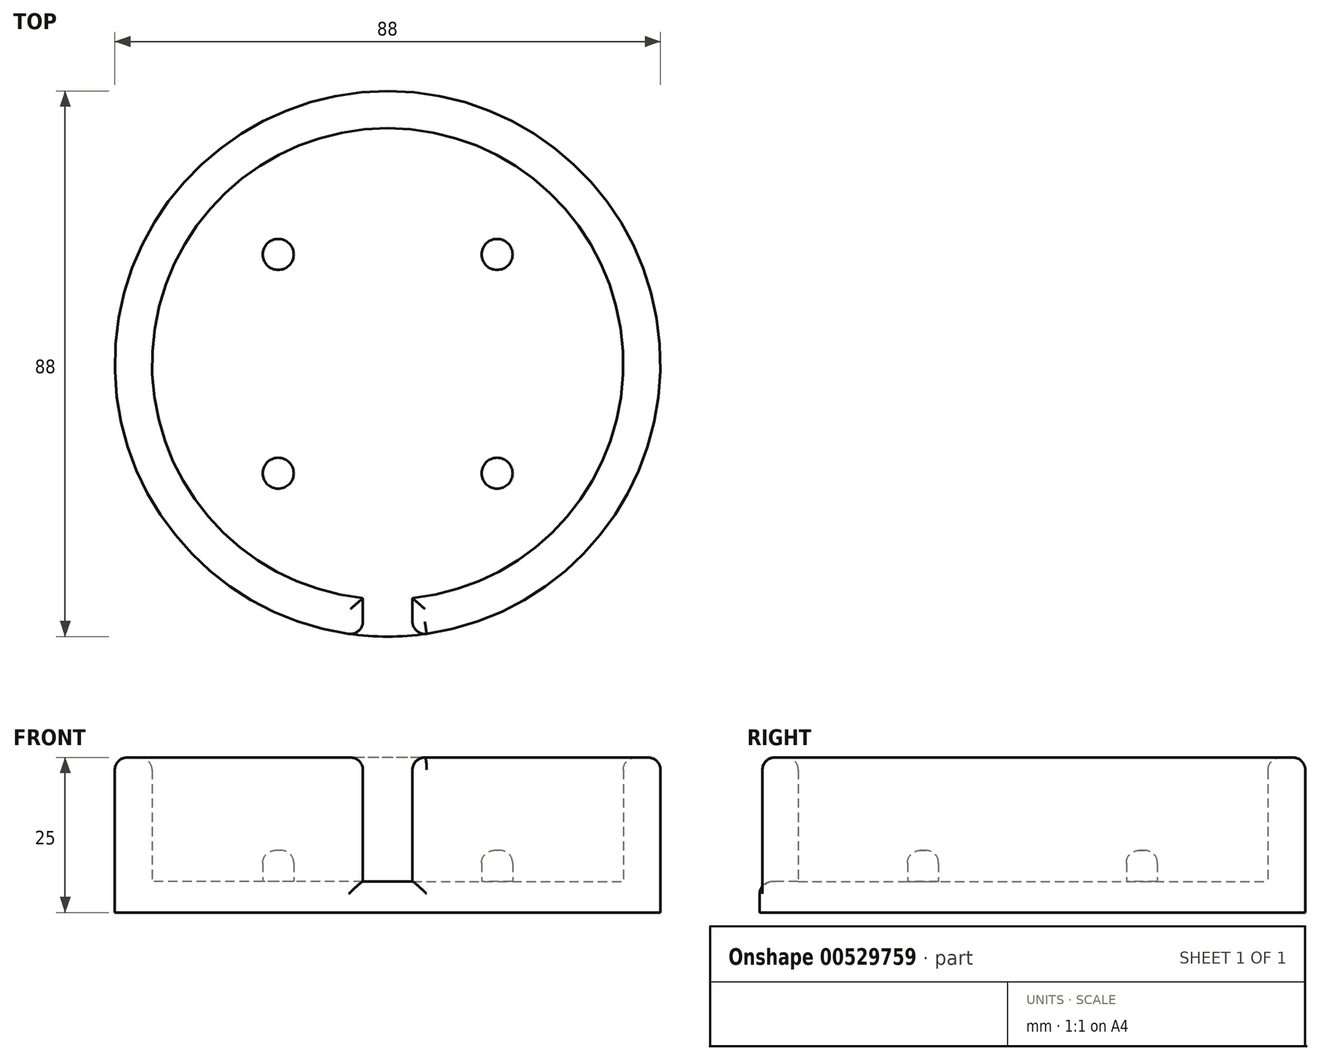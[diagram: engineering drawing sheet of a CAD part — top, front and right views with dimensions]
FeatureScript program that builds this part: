
annotation { "Feature Type Name" : "Feature", "Feature Type Description" : "" }
export const myFeature = defineFeature(function(context is Context, id is Id, definition is map)
    precondition{}
    {
        {
            var Q0;
            Q0=qCreatedBy(makeId("Top.planeOp"),FACE);
            var sketch = newSketch(context, id + "F0", { "sketchPlane" : qUnion([Q0])});
            skCircle(sketch, "E0", {"center": v(0, 0) * mm, "radius": 38 * mm});
            skCircle(sketch, "E1", {"center": v(0, 0) * mm, "radius": 44 * mm});
            skSolve(sketch);
        }
        {
            var Q0;
            Q0 = qSketchRegion(id + "F0", true);
            extrude(context, id + "F1", {"entities" : qUnion([Q0]), "depth" : 25 * mm, "offsetDistance" : 25 * mm});
        }
        {
            var Q0;
            Q0=qCreatedBy(makeId("Top.planeOp"),FACE);
            var sketch = newSketch(context, id + "F2", { "sketchPlane" : qUnion([Q0])});
            skLineSegment(sketch, "E2.bottom", {"start": v(-4, -37.79) * mm, "end": v(4, -37.79) * mm});
            skLineSegment(sketch, "E2.top", {"start": v(-4, -47.79) * mm, "end": v(4, -47.79) * mm});
            skLineSegment(sketch, "E2.left", {"start": v(-4, -37.79) * mm, "end": v(-4, -47.79) * mm});
            skLineSegment(sketch, "E2.right", {"start": v(4, -37.79) * mm, "end": v(4, -47.79) * mm});
            skSolve(sketch);
        }
        {
            var Q0;
            Q0 = qSketchRegion(id + "F2", true);
            extrude(context, id + "F3", {"entities" : qUnion([Q0]), "operationType" : NewBodyOperationType.REMOVE, "endBound" : BoundingType.THROUGH_ALL, "depth" : 25 * mm, "offsetDistance" : 25 * mm});
        }
        {
            var Q0;
            Q0=qCreatedBy(makeId("Top.planeOp"),FACE);
            var sketch = newSketch(context, id + "F4", { "sketchPlane" : qUnion([Q0])});
            skCircle(sketch, "E3", {"center": v(17.65, -17.65) * mm, "radius": 2.5 * mm});
            skCircle(sketch, "E4", {"center": v(17.65, 17.65) * mm, "radius": 2.5 * mm});
            skCircle(sketch, "E5", {"center": v(-17.65, 17.65) * mm, "radius": 2.5 * mm});
            skCircle(sketch, "E6", {"center": v(-17.65, -17.65) * mm, "radius": 2.5 * mm});
            skSolve(sketch);
        }
        {
            var Q0;
            Q0=qCreatedBy(makeId("Top.planeOp"),FACE);
            var sketch = newSketch(context, id + "F5", { "sketchPlane" : qUnion([Q0])});
            skCircle(sketch, "E7", {"center": v(0, 0) * mm, "radius": 44 * mm});
            skSolve(sketch);
        }
        {
            var Q0;
            Q0 = qSketchRegion(id + "F5", true);
            extrude(context, id + "F6", {"entities" : qUnion([Q0]), "operationType" : NewBodyOperationType.ADD, "depth" : 5 * mm, "offsetDistance" : 25 * mm});
        }
        {
            var Q0;
            Q0 = qSketchRegion(id + "F4", true);
            extrude(context, id + "F7", {"entities" : qUnion([Q0]), "operationType" : NewBodyOperationType.ADD, "depth" : 10 * mm, "offsetDistance" : 25 * mm});
        }
        {
            var Q0;
            Q0=makeQuery(id+"F6.opExtrude","CAP_EDGE",EDGE,{"disambiguationData":[OSD([sQuery(id+"F5.wireOp",EDGE,"E7")])],"isStart":false});
            var Q1;
            Q1=makeQuery(id+"F3.boolean.opBoolean","INTERSECT",EDGE,{"derivedFrom":[makeQuery(id+"F1.opExtrude","SWEPT_FACE",FACE,{"disambiguationData":[OSD([sQuery(id+"F0.wireOp",EDGE,"E1")])]}),makeQuery(id+"F3.opExtrude","SWEPT_FACE",FACE,{"disambiguationData":[OSD([sQuery(id+"F2.wireOp",EDGE,"E2.right")])]})]});
            var Q2;
            Q2=makeQuery(id+"F3.boolean.opBoolean","INTERSECT",EDGE,{"derivedFrom":[makeQuery(id+"F1.opExtrude","SWEPT_FACE",FACE,{"disambiguationData":[OSD([sQuery(id+"F0.wireOp",EDGE,"E1")])]}),makeQuery(id+"F3.opExtrude","SWEPT_FACE",FACE,{"disambiguationData":[OSD([sQuery(id+"F2.wireOp",EDGE,"E2.left")])]})]});
            var Q3;
            Q3=makeQuery(id+"F3.boolean.opBoolean","COPY",EDGE,{"derivedFrom":makeQuery(id+"F3.opExtrude","SWEPT_EDGE",EDGE,{"disambiguationData":[OSD([sQuery(id+"F2.wireOp",EDGE,"E2.bottom"),sQuery(id+"F2.wireOp",EDGE,"E2.right")])]})});
            var Q4;
            Q4=makeQuery(id+"F3.boolean.opBoolean","COPY",EDGE,{"derivedFrom":makeQuery(id+"F3.opExtrude","SWEPT_EDGE",EDGE,{"disambiguationData":[OSD([sQuery(id+"F2.wireOp",EDGE,"E2.bottom"),sQuery(id+"F2.wireOp",EDGE,"E2.left")])]})});
            var Q5;
            Q5=makeQuery(id+"F7.opExtrude","CAP_FACE",FACE,{"disambiguationData":[OSD([sQuery(id+"F4.wireOp",EDGE,"E3")])],"isStart":false});
            var Q6;
            Q6=makeQuery(id+"F7.opExtrude","CAP_EDGE",EDGE,{"disambiguationData":[OSD([sQuery(id+"F4.wireOp",EDGE,"E6")])],"isStart":false});
            var Q7;
            Q7=makeQuery(id+"F7.opExtrude","CAP_EDGE",EDGE,{"disambiguationData":[OSD([sQuery(id+"F4.wireOp",EDGE,"E5")])],"isStart":false});
            var Q8;
            Q8=makeQuery(id+"F7.opExtrude","CAP_EDGE",EDGE,{"disambiguationData":[OSD([sQuery(id+"F4.wireOp",EDGE,"E4")])],"isStart":false});
            var Q9;
            Q9=makeQuery(id+"F3.boolean.opBoolean","INTERSECT",EDGE,{"derivedFrom":[makeQuery(id+"F1.opExtrude","CAP_FACE",FACE,{"disambiguationData":[OSD([sQuery(id+"F0.wireOp",EDGE,"E0"),sQuery(id+"F0.wireOp",EDGE,"E1")])],"isStart":false}),makeQuery(id+"F3.opExtrude","SWEPT_FACE",FACE,{"disambiguationData":[OSD([sQuery(id+"F2.wireOp",EDGE,"E2.left")])]})]});
            var Q10;
            Q10=makeQuery(id+"F3.boolean.opBoolean","INTERSECT",EDGE,{"derivedFrom":[makeQuery(id+"F1.opExtrude","CAP_FACE",FACE,{"disambiguationData":[OSD([sQuery(id+"F0.wireOp",EDGE,"E0"),sQuery(id+"F0.wireOp",EDGE,"E1")])],"isStart":false}),makeQuery(id+"F3.opExtrude","SWEPT_FACE",FACE,{"disambiguationData":[OSD([sQuery(id+"F2.wireOp",EDGE,"E2.right")])]})]});
            var Q11;
            Q11=makeQuery(id+"F1.opExtrude","CAP_EDGE",EDGE,{"disambiguationData":[OSD([sQuery(id+"F0.wireOp",EDGE,"E0")])],"isStart":false});
            var Q12;
            Q12=makeQuery(id+"F1.opExtrude","CAP_EDGE",EDGE,{"disambiguationData":[OSD([sQuery(id+"F0.wireOp",EDGE,"E1")])],"isStart":false});
            fillet(context, id + "F8", {"entities" : qUnion([Q0, Q1, Q2, Q3, Q4, Q5, Q6, Q7, Q8, Q9, Q10, Q11, Q12]), "radius" : 2 * mm, "tangentPropagation" : true, "allowEdgeOverflow" : false});
        }
    });
